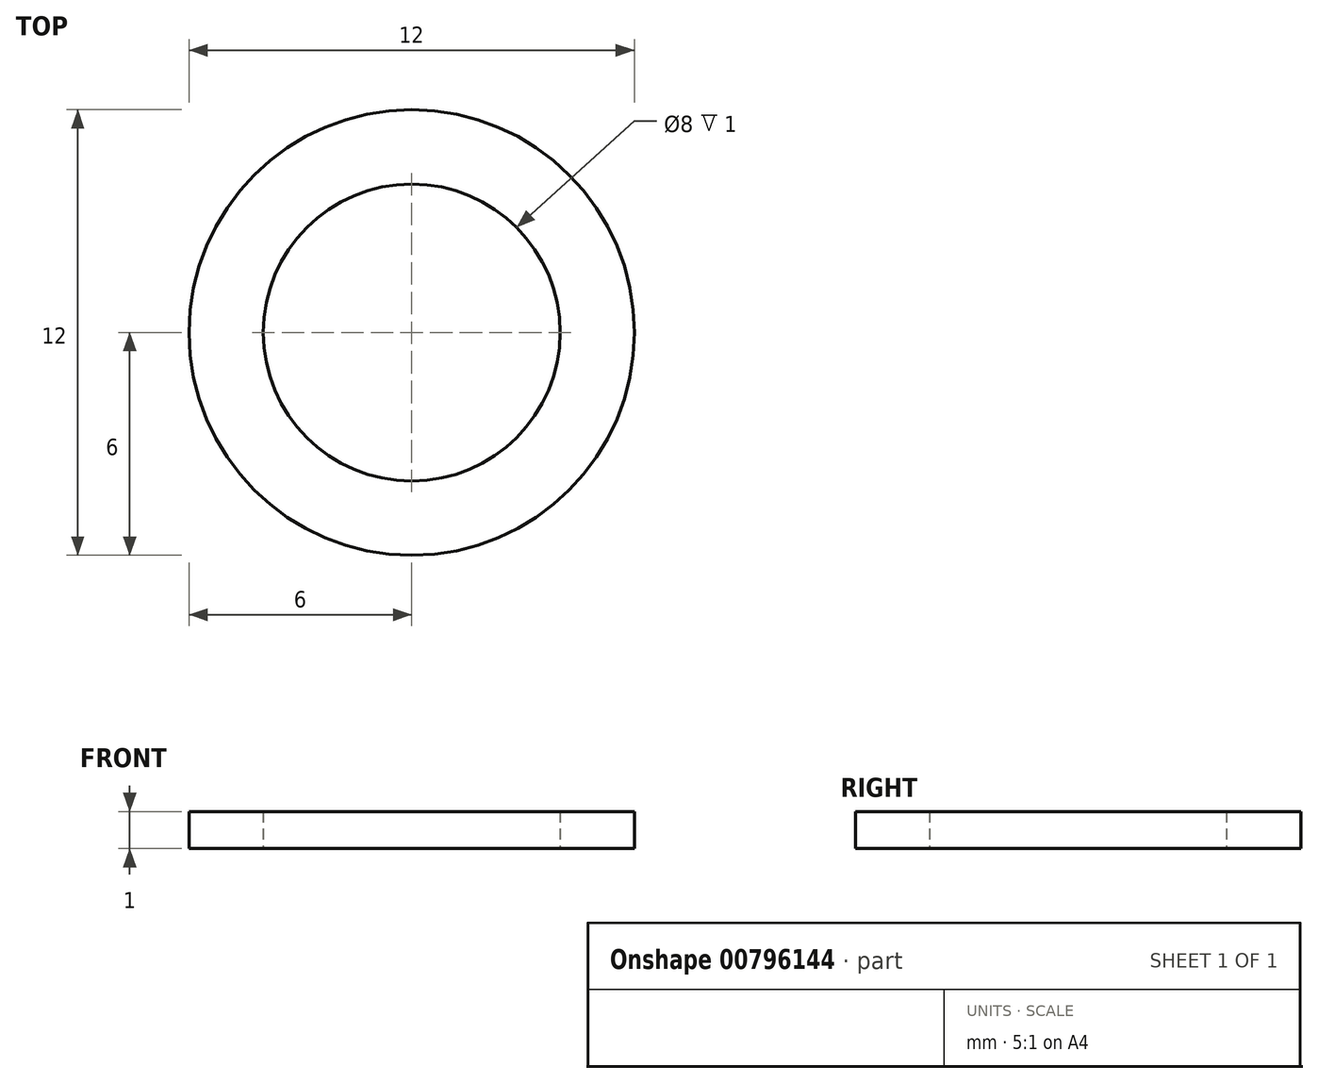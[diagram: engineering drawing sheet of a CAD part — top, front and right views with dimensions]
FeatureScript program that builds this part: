
annotation { "Feature Type Name" : "Feature", "Feature Type Description" : "" }
export const myFeature = defineFeature(function(context is Context, id is Id, definition is map)
    precondition{}
    {
        {
            var Q0;
            Q0=qCreatedBy(makeId("Top.planeOp"),FACE);
            var sketch = newSketch(context, id + "F0", { "sketchPlane" : qUnion([Q0])});
            skCircle(sketch, "E0", {"center": v(0, 0) * mm, "radius": 6 * mm});
            skCircle(sketch, "E1", {"center": v(0, 0) * mm, "radius": 4 * mm});
            skSolve(sketch);
        }
        {
            var Q0;
            Q0=makeQuery(id+"F0.imprint","IMPRINT",FACE,{"disambiguationData":[TD([[makeQuery(id+"F0.imprint","IMPRINT",EDGE,{"derivedFrom":sQuery(id+"F0.wireOp",EDGE,"E0")}),1.0]])]});
            extrude(context, id + "F1", {"entities" : qUnion([Q0]), "depth" : 1 * mm, "offsetDistance" : 25 * mm});
        }
    });
